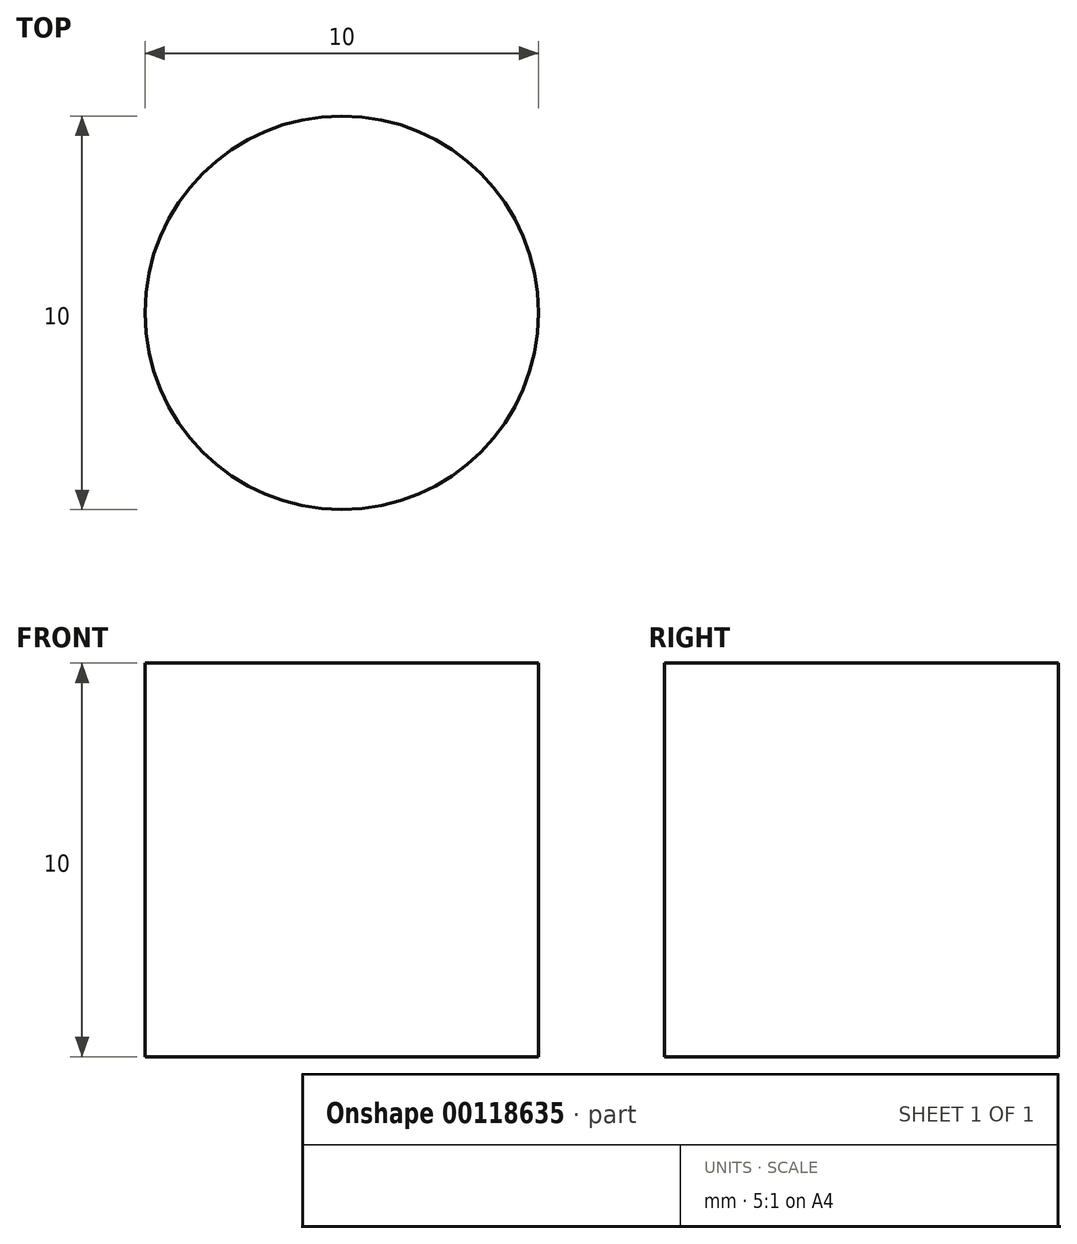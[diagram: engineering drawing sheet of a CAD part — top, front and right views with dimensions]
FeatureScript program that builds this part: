
annotation { "Feature Type Name" : "Feature", "Feature Type Description" : "" }
export const myFeature = defineFeature(function(context is Context, id is Id, definition is map)
    precondition{}
    {
        {
            var Q0;
            Q0=qCreatedBy(makeId("Top.planeOp"),FACE);
            var sketch = newSketch(context, id + "F0", { "sketchPlane" : qUnion([Q0])});
            skCircle(sketch, "E0", {"center": v(0, 0) * mm, "radius": 5 * mm});
            skSolve(sketch);
        }
        {
            var Q0;
            Q0=qSketchRegion(id+"F0",true);
            extrude(context, id + "F1", {"entities" : qUnion([Q0]), "depth" : 10 * mm});
        }
    });
